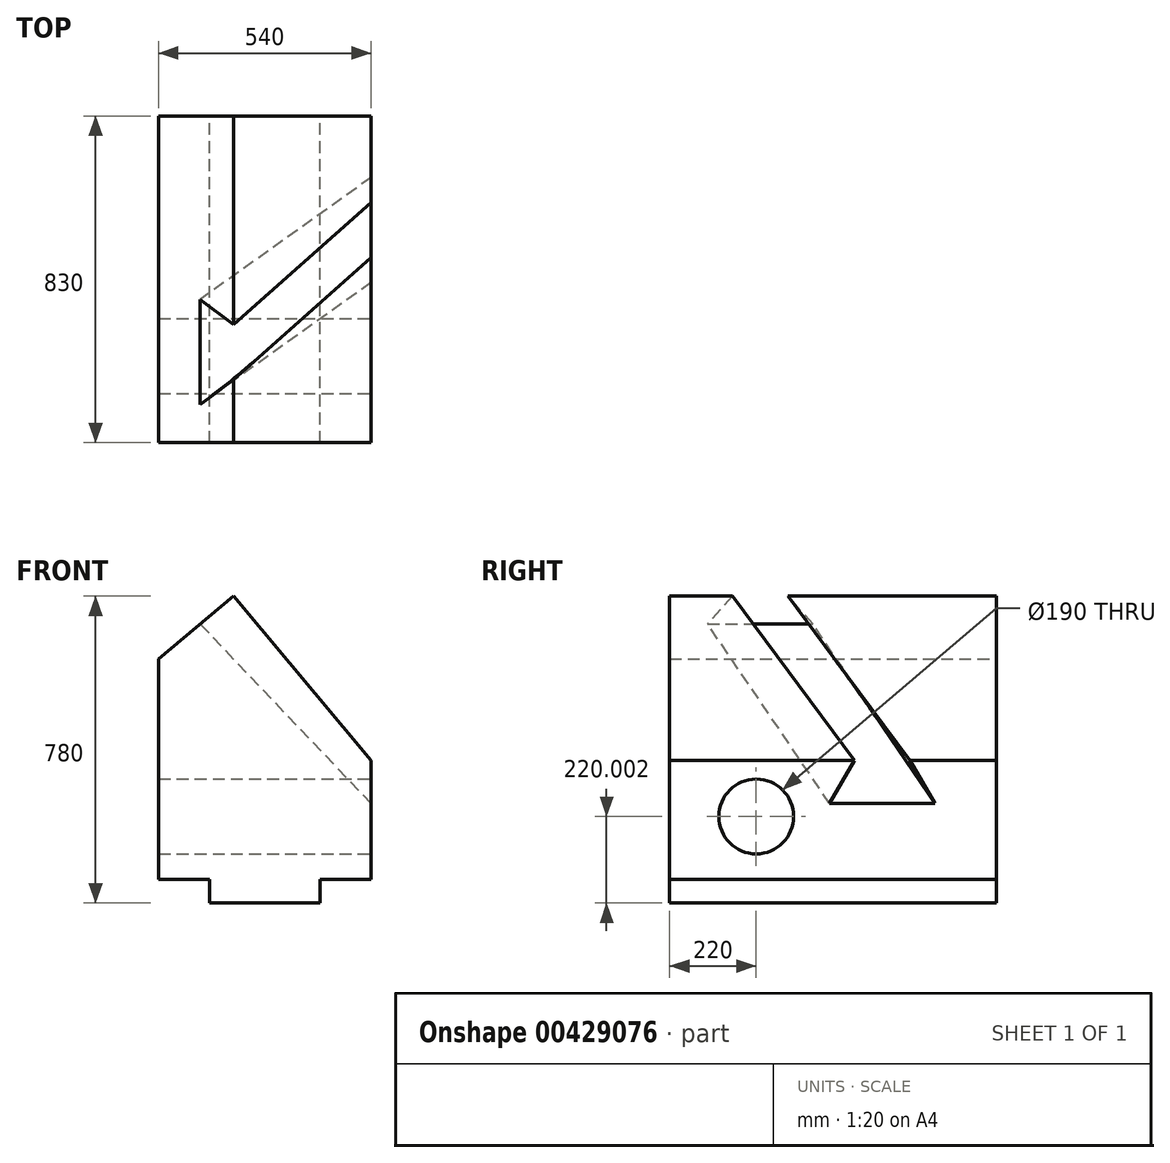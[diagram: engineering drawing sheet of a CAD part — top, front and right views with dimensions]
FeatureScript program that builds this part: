
annotation { "Feature Type Name" : "Feature", "Feature Type Description" : "" }
export const myFeature = defineFeature(function(context is Context, id is Id, definition is map)
    precondition{}
    {
        {
            var Q0;
            Q0=qCreatedBy(makeId("Front.planeOp"),FACE);
            var sketch = newSketch(context, id + "F0", { "sketchPlane" : qUnion([Q0])});
            skLineSegment(sketch, "E0", {"start": v(-835.75, 717.45) * mm, "end": v(-835.75, 156.88) * mm});
            skLineSegment(sketch, "E1", {"start": v(-835.75, 156.88) * mm, "end": v(-705.75, 156.88) * mm});
            skLineSegment(sketch, "E2", {"start": v(-705.75, 156.88) * mm, "end": v(-705.75, 96.88) * mm});
            skLineSegment(sketch, "E3", {"start": v(-705.75, 96.88) * mm, "end": v(-425.75, 96.88) * mm});
            skLineSegment(sketch, "E4", {"start": v(-425.75, 96.88) * mm, "end": v(-425.75, 156.88) * mm});
            skLineSegment(sketch, "E5", {"start": v(-425.75, 156.88) * mm, "end": v(-295.75, 156.88) * mm});
            skLineSegment(sketch, "E6", {"start": v(-295.75, 156.88) * mm, "end": v(-295.75, 459.77) * mm});
            skLineSegment(sketch, "E7", {"start": v(-295.75, 459.77) * mm, "end": v(-645.75, 876.88) * mm});
            skLineSegment(sketch, "E8", {"start": v(-645.75, 876.88) * mm, "end": v(-835.75, 717.45) * mm});
            skLineSegment(sketch, "E9", {"start": v(-645.75, 876.88) * mm, "end": v(216.78, 876.88) * mm, "construction": true});
            skSolve(sketch);
        }
        {
            var Q0;
            Q0=makeQuery(id+"F0.imprint","IMPRINT",FACE,{"disambiguationData":[TD([[makeQuery(id+"F0.imprint","IMPRINT",EDGE,{"derivedFrom":sQuery(id+"F0.wireOp",EDGE,"E0")}),1.0]])]});
            extrude(context, id + "F1", {"entities" : qUnion([Q0]), "depth" : 830 * mm});
        }
        {
            var Q0;
            Q0=makeQuery(id+"F1.opExtrude","SWEPT_FACE",FACE,{"disambiguationData":[OSD([sQuery(id+"F0.wireOp",EDGE,"E6")])]});
            var sketch = newSketch(context, id + "F2", { "sketchPlane" : qUnion([Q0])});
            skLineSegment(sketch, "E10", {"start": v(-360, 459.77) * mm, "end": v(-423.5, 349.77) * mm});
            skLineSegment(sketch, "E11", {"start": v(-423.5, 349.77) * mm, "end": v(-156.5, 349.77) * mm});
            skLineSegment(sketch, "E12", {"start": v(-156.5, 349.77) * mm, "end": v(-220, 459.77) * mm});
            skCircle(sketch, "E13", {"center": v(-610, 316.88) * mm, "radius": 95 * mm});
            skSolve(sketch);
        }
        {
            var Q0;
            Q0=makeQuery(id+"F1.opExtrude","SWEPT_FACE",FACE,{"disambiguationData":[OSD([sQuery(id+"F0.wireOp",EDGE,"E8")])]});
            var sketch = newSketch(context, id + "F3", { "sketchPlane" : qUnion([Q0])});
            skLineSegment(sketch, "E14", {"start": v(68.97, -670) * mm, "end": v(-41.03, -733.5) * mm});
            skLineSegment(sketch, "E15", {"start": v(-41.03, -733.5) * mm, "end": v(-41.03, -466.5) * mm});
            skLineSegment(sketch, "E16", {"start": v(-41.03, -466.5) * mm, "end": v(68.97, -530) * mm});
            skSolve(sketch);
        }
        {
            var Q1;
            {var subQ0=sQuery(id+"F2.wireOp",EDGE,"E10");Q1=makeQuery(id+"F2.imprint","IMPRINT",FACE,{"disambiguationData":[TD([[makeQuery(id+"F2.imprint","IMPRINT",EDGE,{"derivedFrom":subQ0}),1.0]])]});}
            var Q2;
            {var subQ0=sQuery(id+"F3.wireOp",EDGE,"E14");Q2=makeQuery(id+"F3.imprint","IMPRINT",FACE,{"disambiguationData":[TD([[makeQuery(id+"F3.imprint","IMPRINT",EDGE,{"derivedFrom":subQ0}),-1.0]])]});}
            loft(context, id + "F4", {"operationType" : NewBodyOperationType.REMOVE, "sheetProfilesArray" : [{ "sheetProfileEntities" : qUnion([Q1]) }, { "sheetProfileEntities" : qUnion([Q2]) }]});
        }
        {
            var Q0;
            Q0=makeQuery(id+"F2.imprint","IMPRINT",FACE,{"disambiguationData":[TD([[makeQuery(id+"F2.imprint","IMPRINT",EDGE,{"derivedFrom":sQuery(id+"F2.wireOp",EDGE,"E13")}),1.0]])]});
            extrude(context, id + "F5", {"entities" : qUnion([Q0]), "operationType" : NewBodyOperationType.REMOVE, "endBound" : BoundingType.THROUGH_ALL, "oppositeDirection" : true, "depth" : 25 * mm});
        }
    });
